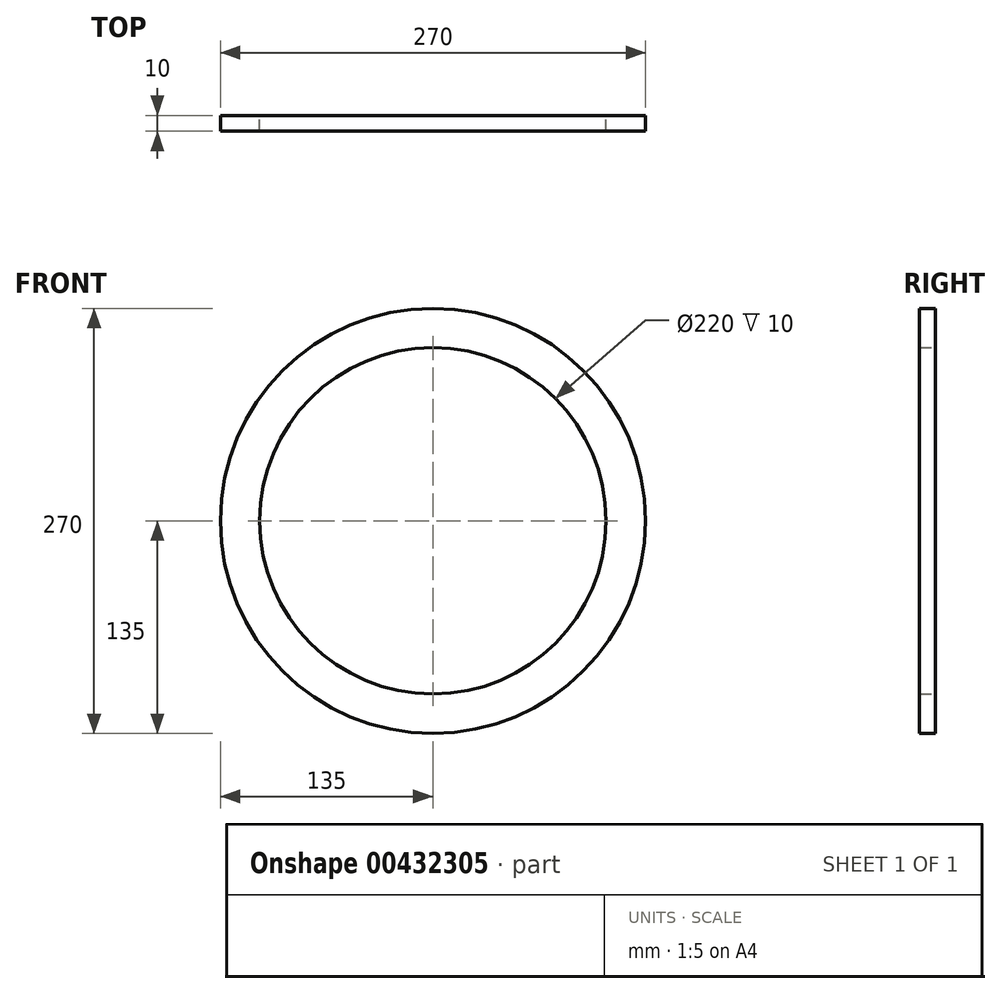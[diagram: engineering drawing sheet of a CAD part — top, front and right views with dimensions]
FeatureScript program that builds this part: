
annotation { "Feature Type Name" : "Feature", "Feature Type Description" : "" }
export const myFeature = defineFeature(function(context is Context, id is Id, definition is map)
    precondition{}
    {
        {
            var Q0;
            Q0=qCreatedBy(makeId("Front.planeOp"),FACE);
            var sketch = newSketch(context, id + "F0", { "sketchPlane" : qUnion([Q0])});
            skCircle(sketch, "E0", {"center": v(0, 0) * mm, "radius": 135 * mm});
            skCircle(sketch, "E1", {"center": v(0, 0) * mm, "radius": 110 * mm});
            skSolve(sketch);
        }
        {
            var Q0;
            Q0=makeQuery(id+"F0.imprint","IMPRINT",FACE,{"disambiguationData":[TD([[makeQuery(id+"F0.imprint","IMPRINT",EDGE,{"derivedFrom":sQuery(id+"F0.wireOp",EDGE,"E0")}),1.0]])]});
            var Q1;
            Q1=makeQuery(id+"F0.imprint","IMPRINT",FACE,{"disambiguationData":[TD([[makeQuery(id+"F0.imprint","IMPRINT",EDGE,{"derivedFrom":sQuery(id+"F0.wireOp",EDGE,"E1")}),-1.0]])]});
            extrude(context, id + "F1", {"entities" : qUnion([Q0, Q1]), "depth" : 10 * mm});
        }
    });
